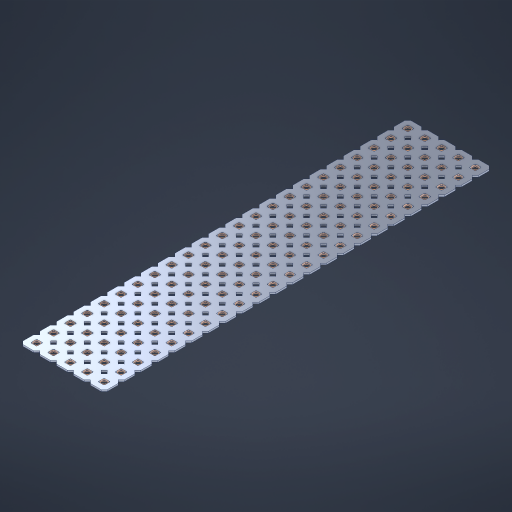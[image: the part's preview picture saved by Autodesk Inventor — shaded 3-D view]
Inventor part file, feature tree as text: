
AUTODESK INVENTOR PART (.ipt)
format: ipt  version: 2023 (Build 270158000, 158)  size: 1,591,808 bytes
history: native  units: in
note: dims shown in document units (in); Inventor stores cm internally (conversion verified against a paired STEP export)
features: other x116, extrude x114, sketch x2, pattern_linear x1
ambient origin geometry x8: Origin, YZ Plane, XZ Plane, XY Plane, X Axis, Y Axis, Z Axis, Center Point
bodies: Solid1 (feature_tree), Body (feature_tree)
feature tree (233):
  pattern_linear  "Rectangular Pattern1"  Spacing1=0.09in  [1 undecoded]
  sketch  "Sketch1"  dims[d1=0.5in]
  sketch  "Sketch2"  dims[d2=0.182in d3=0.09in d4=0.09in d5=0.09in d6=0.09in d7=0.09in d8=0.09in d9=0.09in d10=0.09in d11=0.02in d13=0.0in d14=0.172in d15=0.0625in d16=0.0in d19=0.5in d22=0.5in]
  other  "Srf1"
  other  "Srf126"
  other  "Srf127"
  other  "Srf128"
  other  "Srf129"
  other  "Srf130"
  other  "Srf131"
  other  "Srf250"
  other  "Srf251"
  other  "Srf252"
  other  "Srf253"
  other  "Srf254"
  other  "Srf255"
  other  "Srf256"
  other  "Srf257"
  other  "Srf258"
  other  "Srf259"
  other  "Srf260"
  other  "Srf261"
  other  "Srf262"
  other  "Srf263"
  other  "Srf264"
  other  "Srf265"
  other  "Srf268"
  other  "Srf269"
  other  "Srf270"
  other  "Srf271"
  other  "Srf272"
  other  "Srf273"
  other  "Srf274"
  other  "Srf275"
  other  "Srf276"
  other  "Srf277"
  other  "Srf278"
  other  "Srf279"
  other  "Srf280"
  other  "Srf281"
  other  "Srf282"
  other  "Srf283"
  other  "Srf284"
  other  "Srf285"
  other  "Srf286"
  other  "Srf287"
  other  "Srf288"
  other  "Srf289"
  other  "Srf290"
  other  "Srf293"
  other  "Srf294"
  other  "Srf295"
  other  "Srf296"
  other  "Srf297"
  other  "Srf298"
  other  "Srf299"
  other  "Srf300"
  other  "Srf301"
  other  "Srf302"
  other  "Srf303"
  other  "Srf304"
  other  "Srf305"
  other  "Srf306"
  other  "Srf307"
  other  "Srf308"
  other  "Srf309"
  other  "Srf310"
  other  "Srf311"
  other  "Srf312"
  other  "Srf313"
  other  "Srf314"
  other  "Srf315"
  other  "Srf318"
  other  "Srf319"
  other  "Srf320"
  other  "Srf321"
  other  "Srf322"
  other  "Srf323"
  other  "Srf324"
  other  "Srf325"
  other  "Srf326"
  other  "Srf327"
  other  "Srf328"
  other  "Srf329"
  other  "Srf330"
  other  "Srf331"
  other  "Srf332"
  other  "Srf333"
  other  "Srf334"
  other  "Srf335"
  other  "Srf336"
  other  "Srf337"
  other  "Srf338"
  other  "Srf339"
  other  "Srf340"
  other  "Srf343"
  other  "Srf344"
  other  "Srf345"
  other  "Srf346"
  other  "Srf347"
  other  "Srf348"
  other  "Srf349"
  other  "Srf350"
  other  "Srf351"
  other  "Srf352"
  other  "Srf353"
  other  "Srf354"
  other  "Srf355"
  other  "Srf356"
  other  "Srf357"
  other  "Srf358"
  other  "Srf359"
  other  "Srf360"
  other  "Srf361"
  other  "Srf362"
  other  "Srf363"
  other  "Srf364"
  other  "Srf365"
  other  "Circle"
  extrude  "ExtrusionSrf126"  Depth=0.09in
  extrude  "ExtrusionSrf127"  Depth=0.09in
  extrude  "ExtrusionSrf128"  Depth=0.09in
  extrude  "ExtrusionSrf129"  Depth=0.09in
  extrude  "ExtrusionSrf130"  Depth=0.09in
  extrude  "ExtrusionSrf131"  Depth=0.09in
  extrude  "ExtrusionSrf250"  Depth=0.09in
  extrude  "ExtrusionSrf251"  Depth=0.02in
  extrude  "ExtrusionSrf252"  TaperAngle=0.0deg  [1 undecoded]
  extrude  "ExtrusionSrf253"  Depth=0.5in
  extrude  "ExtrusionSrf254"  Depth=0.5in TaperAngle=0.0deg
  extrude  "ExtrusionSrf255"  Depth=0.5in
  extrude  "ExtrusionSrf256"  Depth=0.5in
  extrude  "ExtrusionSrf257"  [1 undecoded]
  extrude  "ExtrusionSrf258"  [1 undecoded]
  extrude  "ExtrusionSrf259"  [1 undecoded]
  extrude  "ExtrusionSrf260"  [1 undecoded]
  extrude  "ExtrusionSrf261"  [1 undecoded]
  extrude  "ExtrusionSrf262"  [1 undecoded]
  extrude  "ExtrusionSrf263"  [1 undecoded]
  extrude  "ExtrusionSrf264"  [1 undecoded]
  extrude  "ExtrusionSrf265"  [1 undecoded]
  extrude  "ExtrusionSrf268"  [1 undecoded]
  extrude  "ExtrusionSrf269"  [1 undecoded]
  extrude  "ExtrusionSrf270"  [1 undecoded]
  extrude  "ExtrusionSrf271"  [1 undecoded]
  extrude  "ExtrusionSrf272"  [1 undecoded]
  extrude  "ExtrusionSrf273"  [1 undecoded]
  extrude  "ExtrusionSrf274"  [1 undecoded]
  extrude  "ExtrusionSrf275"  [1 undecoded]
  extrude  "ExtrusionSrf276"  [1 undecoded]
  extrude  "ExtrusionSrf277"  [1 undecoded]
  extrude  "ExtrusionSrf278"  [1 undecoded]
  extrude  "ExtrusionSrf279"  [1 undecoded]
  extrude  "ExtrusionSrf280"  [1 undecoded]
  extrude  "ExtrusionSrf281"  [1 undecoded]
  extrude  "ExtrusionSrf282"  [1 undecoded]
  extrude  "ExtrusionSrf283"  [1 undecoded]
  extrude  "ExtrusionSrf284"  [1 undecoded]
  extrude  "ExtrusionSrf285"  [1 undecoded]
  extrude  "ExtrusionSrf286"  [1 undecoded]
  extrude  "ExtrusionSrf287"  [1 undecoded]
  extrude  "ExtrusionSrf288"  [1 undecoded]
  extrude  "ExtrusionSrf289"  [1 undecoded]
  extrude  "ExtrusionSrf290"  [1 undecoded]
  extrude  "ExtrusionSrf293"  [1 undecoded]
  extrude  "ExtrusionSrf294"  [1 undecoded]
  extrude  "ExtrusionSrf295"  [1 undecoded]
  extrude  "ExtrusionSrf296"  [1 undecoded]
  extrude  "ExtrusionSrf297"  [1 undecoded]
  extrude  "ExtrusionSrf298"  [1 undecoded]
  extrude  "ExtrusionSrf299"  [1 undecoded]
  extrude  "ExtrusionSrf300"  [1 undecoded]
  extrude  "ExtrusionSrf301"  [1 undecoded]
  extrude  "ExtrusionSrf302"  [1 undecoded]
  extrude  "ExtrusionSrf303"  [1 undecoded]
  extrude  "ExtrusionSrf304"  [1 undecoded]
  extrude  "ExtrusionSrf305"  [1 undecoded]
  extrude  "ExtrusionSrf306"  [1 undecoded]
  extrude  "ExtrusionSrf307"  [1 undecoded]
  extrude  "ExtrusionSrf308"  [1 undecoded]
  extrude  "ExtrusionSrf309"  [1 undecoded]
  extrude  "ExtrusionSrf310"  [1 undecoded]
  extrude  "ExtrusionSrf311"  [1 undecoded]
  extrude  "ExtrusionSrf312"  [1 undecoded]
  extrude  "ExtrusionSrf313"  [1 undecoded]
  extrude  "ExtrusionSrf314"  [1 undecoded]
  extrude  "ExtrusionSrf315"  [1 undecoded]
  extrude  "ExtrusionSrf318"  [1 undecoded]
  extrude  "ExtrusionSrf319"  [1 undecoded]
  extrude  "ExtrusionSrf320"  [1 undecoded]
  extrude  "ExtrusionSrf321"  [1 undecoded]
  extrude  "ExtrusionSrf322"  [1 undecoded]
  extrude  "ExtrusionSrf323"  [1 undecoded]
  extrude  "ExtrusionSrf324"  [1 undecoded]
  extrude  "ExtrusionSrf325"  [1 undecoded]
  extrude  "ExtrusionSrf326"  [1 undecoded]
  extrude  "ExtrusionSrf327"  [1 undecoded]
  extrude  "ExtrusionSrf328"  [1 undecoded]
  extrude  "ExtrusionSrf329"  [1 undecoded]
  extrude  "ExtrusionSrf330"  [1 undecoded]
  extrude  "ExtrusionSrf331"  [1 undecoded]
  extrude  "ExtrusionSrf332"  [1 undecoded]
  extrude  "ExtrusionSrf333"  [1 undecoded]
  extrude  "ExtrusionSrf334"  [1 undecoded]
  extrude  "ExtrusionSrf335"  [1 undecoded]
  extrude  "ExtrusionSrf336"  [1 undecoded]
  extrude  "ExtrusionSrf337"  [1 undecoded]
  extrude  "ExtrusionSrf338"  [1 undecoded]
  extrude  "ExtrusionSrf339"  [1 undecoded]
  extrude  "ExtrusionSrf340"  [1 undecoded]
  extrude  "ExtrusionSrf343"  [1 undecoded]
  extrude  "ExtrusionSrf344"  [1 undecoded]
  extrude  "ExtrusionSrf345"  [1 undecoded]
  extrude  "ExtrusionSrf346"  [1 undecoded]
  extrude  "ExtrusionSrf347"  [1 undecoded]
  extrude  "ExtrusionSrf348"  [1 undecoded]
  extrude  "ExtrusionSrf349"  [1 undecoded]
  extrude  "ExtrusionSrf350"  [1 undecoded]
  extrude  "ExtrusionSrf351"  [1 undecoded]
  extrude  "ExtrusionSrf352"  [1 undecoded]
  extrude  "ExtrusionSrf353"  [1 undecoded]
  extrude  "ExtrusionSrf354"  [1 undecoded]
  extrude  "ExtrusionSrf355"  [1 undecoded]
  extrude  "ExtrusionSrf356"  [1 undecoded]
  extrude  "ExtrusionSrf357"  [1 undecoded]
  extrude  "ExtrusionSrf358"  [1 undecoded]
  extrude  "ExtrusionSrf359"  [1 undecoded]
  extrude  "ExtrusionSrf360"  [1 undecoded]
  extrude  "ExtrusionSrf361"  [1 undecoded]
  extrude  "ExtrusionSrf362"  [1 undecoded]
  extrude  "ExtrusionSrf363"  [1 undecoded]
  extrude  "ExtrusionSrf364"  [1 undecoded]
  extrude  "ExtrusionSrf365"  [1 undecoded]
note: 103 required parameter values undecoded (feature->parameter linkage not recoverable at this tier; creation-order binding heuristic only, values carry confidence <= 0.55)
